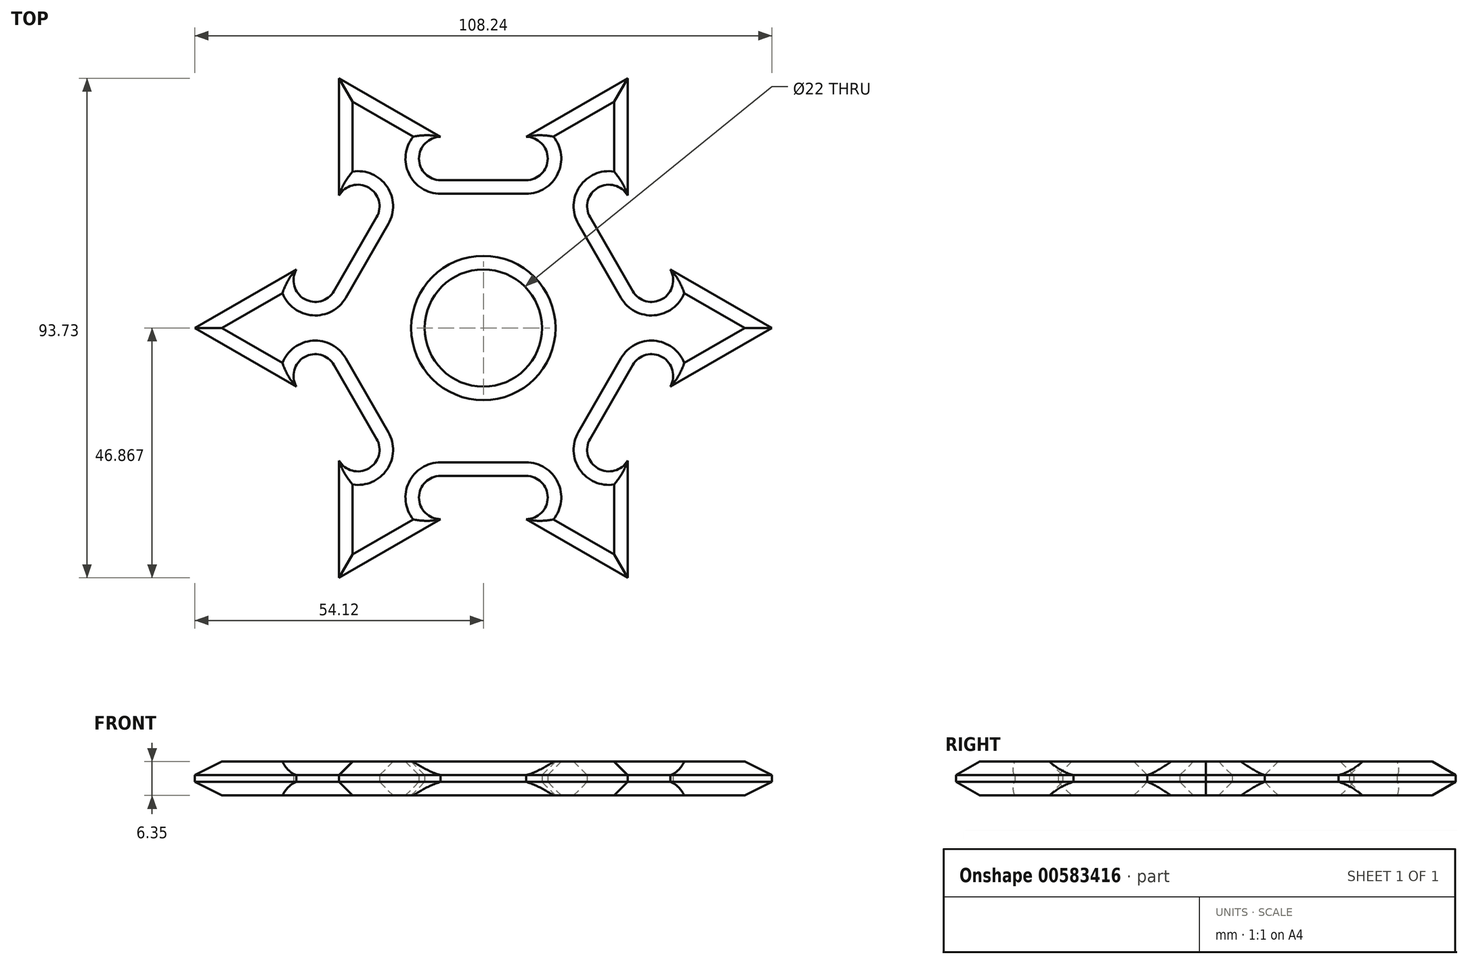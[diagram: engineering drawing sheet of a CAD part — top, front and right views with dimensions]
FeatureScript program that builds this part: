
annotation { "Feature Type Name" : "Feature", "Feature Type Description" : "" }
export const myFeature = defineFeature(function(context is Context, id is Id, definition is map)
    precondition{}
    {
        {
            var Q0;
            Q0=qCreatedBy(makeId("Top.planeOp"),FACE);
            var sketch = newSketch(context, id + "F0", { "sketchPlane" : qUnion([Q0])});
            skPoint(sketch, "E0.0.midPoint", {"position": v(-10.57, -11.73) * mm});
            skLineSegment(sketch, "E1", {"start": v(-38.6, 9.07) * mm, "end": v(-30.59, -4.8) * mm});
            skLineSegment(sketch, "E2", {"start": v(-38.6, 22.94) * mm, "end": v(-30.59, 36.81) * mm});
            skLineSegment(sketch, "E3", {"start": v(-18.58, 43.75) * mm, "end": v(-2.56, 43.75) * mm});
            skLineSegment(sketch, "E4", {"start": v(9.45, 36.81) * mm, "end": v(17.46, 22.94) * mm});
            skLineSegment(sketch, "E5", {"start": v(17.46, 9.07) * mm, "end": v(9.45, -4.8) * mm});
            skLineSegment(sketch, "E6", {"start": v(-18.58, -11.73) * mm, "end": v(-2.56, -11.73) * mm});
            skArc(sketch, "E7", {"start": v(-30.59, 36.81) * mm, "mid": v(-32.08, 42.36) * mm, "end": v(-37.63, 40.88) * mm});
            skArc(sketch, "E8", {"start": v(-18.58, 51.87) * mm, "mid": v(-22.64, 47.8) * mm, "end": v(-18.58, 43.75) * mm});
            skArc(sketch, "E9", {"start": v(-2.56, 43.75) * mm, "mid": v(1.5, 47.8) * mm, "end": v(-2.56, 51.87) * mm});
            skArc(sketch, "E10", {"start": v(16.49, 40.88) * mm, "mid": v(10.94, 42.36) * mm, "end": v(9.45, 36.81) * mm});
            skArc(sketch, "E11", {"start": v(17.46, 22.94) * mm, "mid": v(23, 21.45) * mm, "end": v(24.5, 27) * mm});
            skArc(sketch, "E12", {"start": v(24.5, 5) * mm, "mid": v(23, 10.56) * mm, "end": v(17.46, 9.07) * mm});
            skArc(sketch, "E13", {"start": v(9.45, -4.8) * mm, "mid": v(10.94, -10.35) * mm, "end": v(16.49, -8.86) * mm});
            skArc(sketch, "E14", {"start": v(-2.56, -19.86) * mm, "mid": v(1.5, -15.8) * mm, "end": v(-2.56, -11.73) * mm});
            skArc(sketch, "E15", {"start": v(-18.58, -11.73) * mm, "mid": v(-22.64, -15.8) * mm, "end": v(-18.58, -19.86) * mm});
            skArc(sketch, "E16", {"start": v(-37.63, -8.86) * mm, "mid": v(-32.08, -10.35) * mm, "end": v(-30.59, -4.8) * mm});
            skArc(sketch, "E17", {"start": v(-38.6, 9.07) * mm, "mid": v(-44.15, 10.56) * mm, "end": v(-45.64, 5) * mm});
            skArc(sketch, "E18", {"start": v(-45.64, 27) * mm, "mid": v(-44.15, 21.45) * mm, "end": v(-38.6, 22.94) * mm});
            skLineSegment(sketch, "E19", {"start": v(6.96, 46.37) * mm, "end": v(16.49, 62.87) * mm});
            skLineSegment(sketch, "E20", {"start": v(-28.1, 46.37) * mm, "end": v(-37.63, 62.87) * mm});
            skLineSegment(sketch, "E21", {"start": v(-45.64, 16) * mm, "end": v(-64.69, 16) * mm});
            skLineSegment(sketch, "E22", {"start": v(-28.1, -14.36) * mm, "end": v(-37.63, -30.86) * mm});
            skLineSegment(sketch, "E23", {"start": v(6.96, -14.36) * mm, "end": v(16.49, -30.86) * mm});
            skLineSegment(sketch, "E24", {"start": v(24.5, 16) * mm, "end": v(43.55, 16) * mm});
            skLineSegment(sketch, "E25", {"start": v(-37.63, 62.87) * mm, "end": v(-37.63, 40.88) * mm});
            skLineSegment(sketch, "E26", {"start": v(-37.63, 62.87) * mm, "end": v(-18.58, 51.87) * mm});
            skLineSegment(sketch, "E27", {"start": v(-45.64, 27) * mm, "end": v(-64.69, 16) * mm});
            skLineSegment(sketch, "E28", {"start": v(-64.69, 16) * mm, "end": v(-45.64, 5) * mm});
            skLineSegment(sketch, "E29", {"start": v(-37.63, -8.86) * mm, "end": v(-37.63, -30.86) * mm});
            skLineSegment(sketch, "E30", {"start": v(-37.63, -30.86) * mm, "end": v(-18.58, -19.86) * mm});
            skLineSegment(sketch, "E31", {"start": v(-2.56, -19.86) * mm, "end": v(16.49, -30.86) * mm});
            skLineSegment(sketch, "E32", {"start": v(16.49, -30.86) * mm, "end": v(16.49, -8.86) * mm});
            skLineSegment(sketch, "E33", {"start": v(43.55, 16) * mm, "end": v(24.5, 5) * mm});
            skLineSegment(sketch, "E34", {"start": v(43.55, 16) * mm, "end": v(24.5, 27) * mm});
            skLineSegment(sketch, "E35", {"start": v(-2.56, 51.87) * mm, "end": v(16.49, 62.87) * mm});
            skLineSegment(sketch, "E36", {"start": v(16.49, 62.87) * mm, "end": v(16.49, 40.88) * mm});
            skCircle(sketch, "E37", {"center": v(-10.57, 16) * mm, "radius": 11 * mm});
            skPoint(sketch, "E37.centerSnap0", {"position": v(-38.6, 16) * mm});
            skPoint(sketch, "E37.centerSnap1", {"position": v(-10.57, 43.75) * mm});
            skLineSegment(sketch, "E38", {"start": v(-37.63, 62.87) * mm, "end": v(43.55, 62.87) * mm});
            skLineSegment(sketch, "E39", {"start": v(43.55, 62.87) * mm, "end": v(43.55, -30.86) * mm});
            skLineSegment(sketch, "E40", {"start": v(43.55, -30.86) * mm, "end": v(-64.69, -30.86) * mm});
            skLineSegment(sketch, "E41", {"start": v(-64.69, -30.86) * mm, "end": v(-64.69, 62.87) * mm});
            skLineSegment(sketch, "E42", {"start": v(-64.69, 62.87) * mm, "end": v(-37.63, 62.87) * mm});
            skSolve(sketch);
        }
        {
            var Q0;
            Q0=makeQuery(id+"F0.imprint","IMPRINT",FACE,{"disambiguationData":[TD([[makeQuery(id+"F0.imprint","IMPRINT",EDGE,{"derivedFrom":sQuery(id+"F0.wireOp",EDGE,"E1")}),1.0]])]});
            extrude(context, id + "F1", {"entities" : qUnion([Q0]), "depth" : 6.35 * mm, "offsetDistance" : 25.4 * mm});
        }
        {
            var Q0;
            Q0=makeQuery(id+"F1.opExtrude","CAP_FACE",FACE,{"disambiguationData":[OSD([sQuery(id+"F0.wireOp",EDGE,"E1"),sQuery(id+"F0.wireOp",EDGE,"E2"),sQuery(id+"F0.wireOp",EDGE,"E3"),sQuery(id+"F0.wireOp",EDGE,"E4"),sQuery(id+"F0.wireOp",EDGE,"E5"),sQuery(id+"F0.wireOp",EDGE,"E6"),sQuery(id+"F0.wireOp",EDGE,"E7"),sQuery(id+"F0.wireOp",EDGE,"E8"),sQuery(id+"F0.wireOp",EDGE,"E9"),sQuery(id+"F0.wireOp",EDGE,"E10"),sQuery(id+"F0.wireOp",EDGE,"E11"),sQuery(id+"F0.wireOp",EDGE,"E12"),sQuery(id+"F0.wireOp",EDGE,"E13"),sQuery(id+"F0.wireOp",EDGE,"E14"),sQuery(id+"F0.wireOp",EDGE,"E15"),sQuery(id+"F0.wireOp",EDGE,"E16"),sQuery(id+"F0.wireOp",EDGE,"E17"),sQuery(id+"F0.wireOp",EDGE,"E18"),sQuery(id+"F0.wireOp",EDGE,"E25"),sQuery(id+"F0.wireOp",EDGE,"E26"),sQuery(id+"F0.wireOp",EDGE,"E27"),sQuery(id+"F0.wireOp",EDGE,"E28"),sQuery(id+"F0.wireOp",EDGE,"E29"),sQuery(id+"F0.wireOp",EDGE,"E30"),sQuery(id+"F0.wireOp",EDGE,"E31"),sQuery(id+"F0.wireOp",EDGE,"E32"),sQuery(id+"F0.wireOp",EDGE,"E33"),sQuery(id+"F0.wireOp",EDGE,"E34"),sQuery(id+"F0.wireOp",EDGE,"E35"),sQuery(id+"F0.wireOp",EDGE,"E36"),sQuery(id+"F0.wireOp",EDGE,"E37")])],"isStart":false});
            var Q1;
            Q1=makeQuery(id+"F1.opExtrude","CAP_FACE",FACE,{"disambiguationData":[OSD([sQuery(id+"F0.wireOp",EDGE,"E1"),sQuery(id+"F0.wireOp",EDGE,"E2"),sQuery(id+"F0.wireOp",EDGE,"E3"),sQuery(id+"F0.wireOp",EDGE,"E4"),sQuery(id+"F0.wireOp",EDGE,"E5"),sQuery(id+"F0.wireOp",EDGE,"E6"),sQuery(id+"F0.wireOp",EDGE,"E7"),sQuery(id+"F0.wireOp",EDGE,"E8"),sQuery(id+"F0.wireOp",EDGE,"E9"),sQuery(id+"F0.wireOp",EDGE,"E10"),sQuery(id+"F0.wireOp",EDGE,"E11"),sQuery(id+"F0.wireOp",EDGE,"E12"),sQuery(id+"F0.wireOp",EDGE,"E13"),sQuery(id+"F0.wireOp",EDGE,"E14"),sQuery(id+"F0.wireOp",EDGE,"E15"),sQuery(id+"F0.wireOp",EDGE,"E16"),sQuery(id+"F0.wireOp",EDGE,"E17"),sQuery(id+"F0.wireOp",EDGE,"E18"),sQuery(id+"F0.wireOp",EDGE,"E25"),sQuery(id+"F0.wireOp",EDGE,"E26"),sQuery(id+"F0.wireOp",EDGE,"E27"),sQuery(id+"F0.wireOp",EDGE,"E28"),sQuery(id+"F0.wireOp",EDGE,"E29"),sQuery(id+"F0.wireOp",EDGE,"E30"),sQuery(id+"F0.wireOp",EDGE,"E31"),sQuery(id+"F0.wireOp",EDGE,"E32"),sQuery(id+"F0.wireOp",EDGE,"E33"),sQuery(id+"F0.wireOp",EDGE,"E34"),sQuery(id+"F0.wireOp",EDGE,"E35"),sQuery(id+"F0.wireOp",EDGE,"E36"),sQuery(id+"F0.wireOp",EDGE,"E37")])],"isStart":true});
            chamfer(context, id + "F2", {"entities" : qUnion([Q0, Q1]), "width" : 2.54 * mm, "tangentPropagation" : true});
        }
    });
